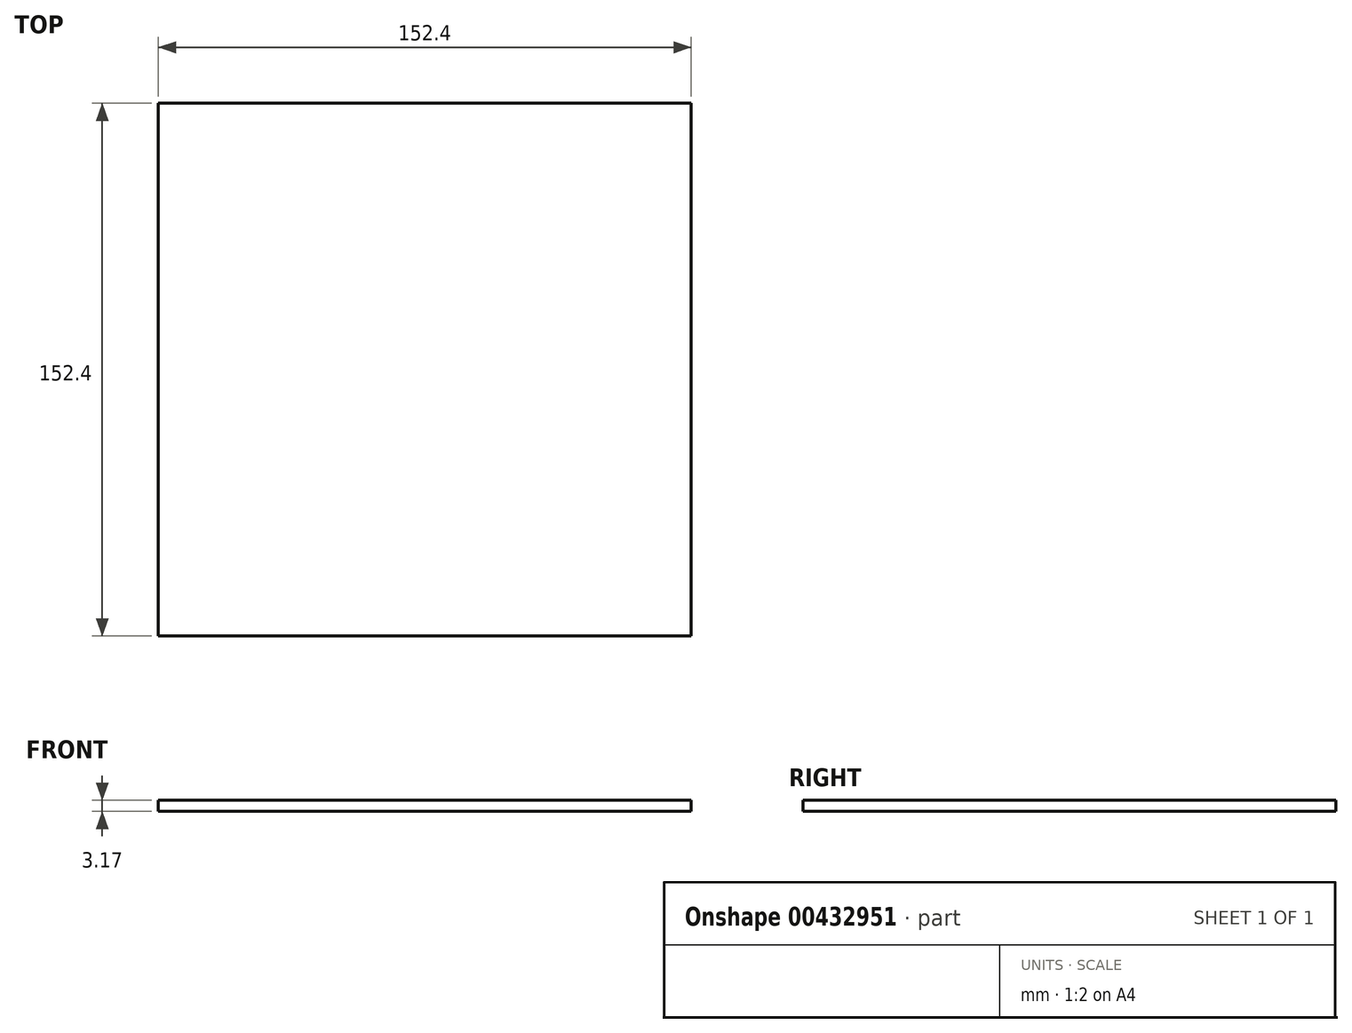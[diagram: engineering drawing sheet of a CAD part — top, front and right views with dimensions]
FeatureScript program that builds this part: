
annotation { "Feature Type Name" : "Feature", "Feature Type Description" : "" }
export const myFeature = defineFeature(function(context is Context, id is Id, definition is map)
    precondition{}
    {
        {
            var Q0;
            Q0=qCreatedBy(makeId("Top.planeOp"),FACE);
            var sketch = newSketch(context, id + "F0", { "sketchPlane" : qUnion([Q0])});
            skLineSegment(sketch, "E0.bottom", {"start": v(76.2, -76.2) * mm, "end": v(-76.2, -76.2) * mm});
            skLineSegment(sketch, "E0.top", {"start": v(76.2, 76.2) * mm, "end": v(-76.2, 76.2) * mm});
            skLineSegment(sketch, "E0.left", {"start": v(76.2, -76.2) * mm, "end": v(76.2, 76.2) * mm});
            skLineSegment(sketch, "E0.right", {"start": v(-76.2, -76.2) * mm, "end": v(-76.2, 76.2) * mm});
            skPoint(sketch, "E0.middle", {"position": v(0, 0) * mm});
            skSolve(sketch);
        }
        {
            var Q0;
            Q0=makeQuery(id+"F0.imprint","IMPRINT",FACE,{"disambiguationData":[TD([[makeQuery(id+"F0.imprint","IMPRINT",EDGE,{"derivedFrom":sQuery(id+"F0.wireOp",EDGE,"E0.bottom")}),-1.0]])]});
            extrude(context, id + "F1", {"entities" : qUnion([Q0]), "depth" : 3.17 * mm});
        }
    });
